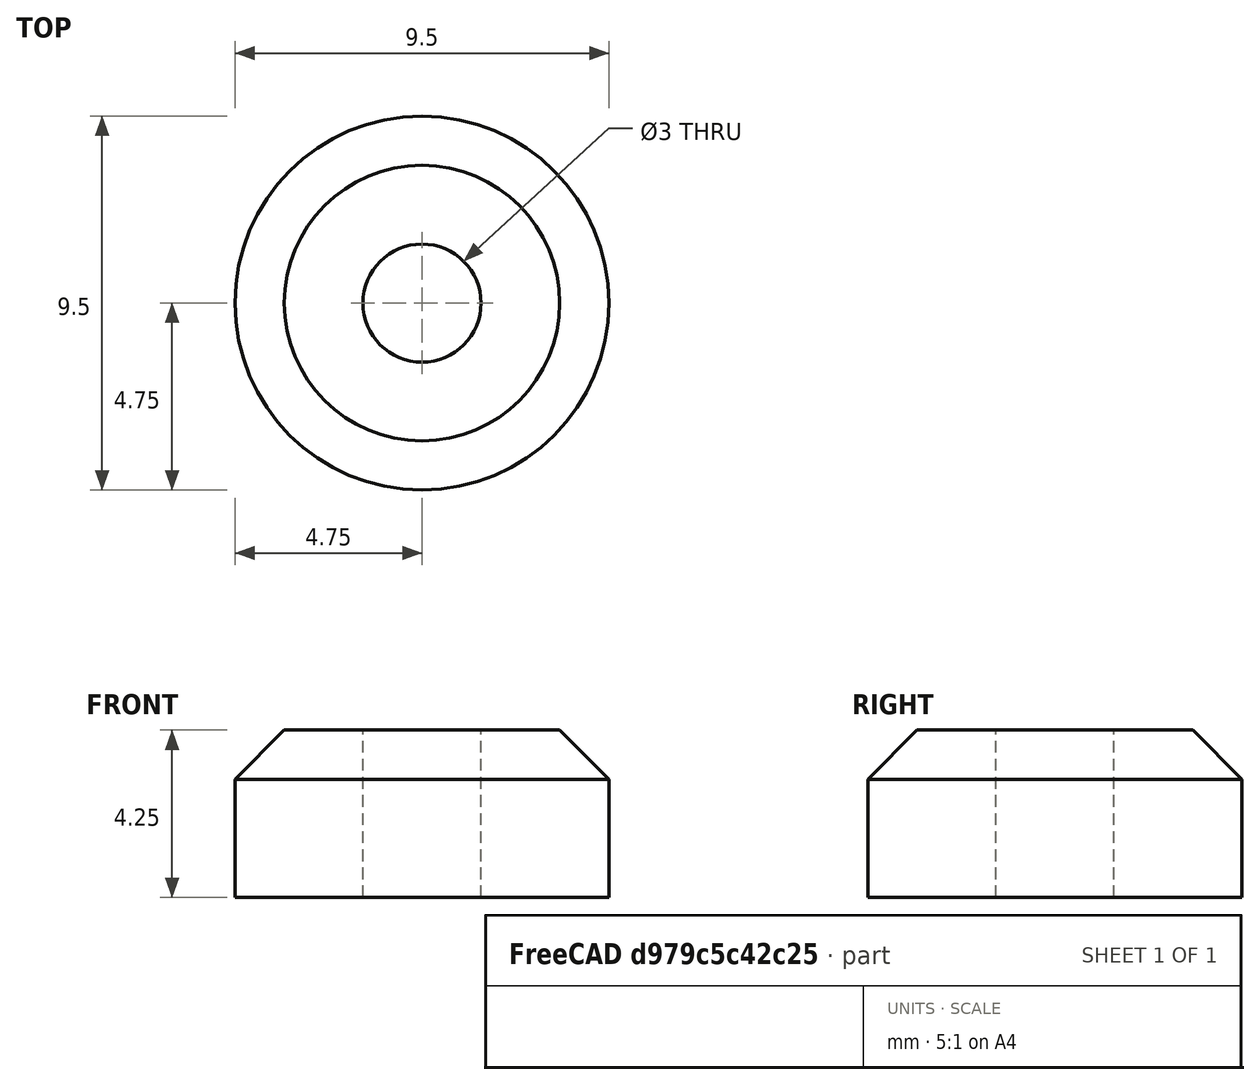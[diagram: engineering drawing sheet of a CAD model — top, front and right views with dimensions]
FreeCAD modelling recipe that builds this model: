
FCSTD DOCUMENT  (FreeCAD 0.20R29410 (Git))
Label: #9_PasiveBearingSpacer
License: All rights reserved
LicenseURL: http://en.wikipedia.org/wiki/All_rights_reserved
objects: Sketcher::SketchObject×1, PartDesign::Revolution×1, PartDesign::Body×1
note: 4 computed .brp shape members not serialized (recipe doc carries the construction recipe); baked Part::Feature solids carry a one-line shape summary decoded from their .brp

FEATURE [Sketcher::SketchObject] Sketch
  FullyConstrained = true
  MapMode = 5
  Placement = pos=(0,0,0) rot=(1,0,0;1.5708rad)
  Support = -> [XZ_Plane]
  sketch-geometry (5):
    g0: LineSegment StartX=1.5 StartY=0 StartZ=0 EndX=4.75 EndY=0 EndZ=0
    g1: LineSegment StartX=4.75 StartY=0 StartZ=0 EndX=4.75 EndY=3 EndZ=0
    g2: LineSegment StartX=4.75 StartY=3 StartZ=0 EndX=3.5 EndY=4.25 EndZ=0
    g3: LineSegment StartX=3.5 StartY=4.25 StartZ=0 EndX=1.5 EndY=4.25 EndZ=0
    g4: LineSegment StartX=1.5 StartY=0 StartZ=0 EndX=1.5 EndY=4.25 EndZ=0
  constraints (15):
    c: PointOnObject(g0,g-1)
    c: PointOnObject(g0,g-1)
    c: Coincident(g1,g0)
    c: Vertical(g1)
    c: Coincident(g2,g1)
    c: DistanceX(g-1,g0) = 4.75
    c: DistanceX(g-1,g2) = 3.5
    c: DistanceY(g0,g2) = 4.25
    c: DistanceY(g0,g1) = 3
    c: DistanceX(g-1,g0) = 1.5
    c: Coincident(g3,g2)
    c: Horizontal(g3)
    c: Coincident(g4,g0)
    c: Vertical(g4)
    c: Coincident(g4,g3)
FEATURE [PartDesign::Revolution] Revolution
  Angle = 360
  Axis = (0,2e-16,1)
  Base = (0,0,0)
  Placement = pos=(0,0,0) rot=(1,0,0;1.5708rad)
  Profile = -> Sketch
  ReferenceAxis = -> Sketch [V_Axis]
  Reversed = true
FEATURE [PartDesign::Body] Body
  Group = -> [Sketch,Revolution]
  Origin = -> Origin
  Tip = -> Revolution
